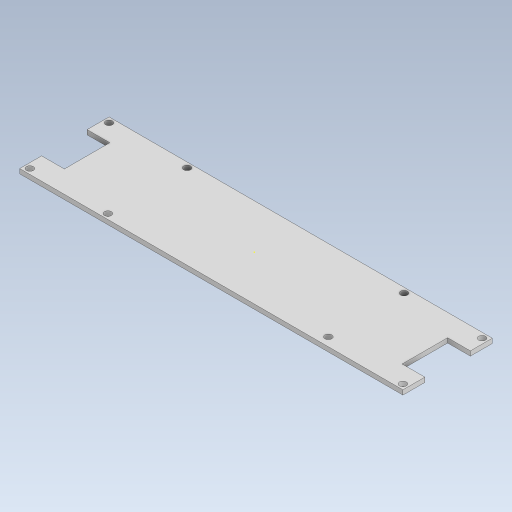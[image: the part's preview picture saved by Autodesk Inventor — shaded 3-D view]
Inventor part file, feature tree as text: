
AUTODESK INVENTOR PART (.ipt)
format: ipt  version: 2023.5 (Build 275446000, 446)  size: 306,176 bytes
history: native  units: in
note: dims shown in document units (in); Inventor stores cm internally (conversion verified against a paired STEP export)
features: extrude x4, sketch x3
ambient origin geometry x8: Origin, YZ Plane, XZ Plane, XY Plane, X Axis, Y Axis, Z Axis, Center Point
bodies: Solid1 (feature_tree)
feature tree (7):
  sketch  "Sketch1"  dims[d0=6.6339in d1=1.5472in]
  extrude  "Extrusion1"  Depth=1.5472in
  extrude  "Extrusion2"  Depth=0.0886in
  extrude  "Extrusion3"  Depth=0.0787in TaperAngle=0.0deg
  sketch  "Sketch3"  dims[d4=0.0886in d5=0.0787in d6=0.0in d7=0.0886in d8=0.0787in d9=0.0in d10=0.7874in d11=0.7874in d12=0.7874in d13=0.7874in d14=0.0787in d15=0.0in d16=0.1181in d17=1.3504in d18=0.1181in d19=0.1181in d20=1.3504in d21=0.1181in d22=0.0787in d23=0.0in]
  extrude  "Extrusion4"  Depth=0.0787in
  sketch  "Sketch2"  dims[d2=0.1181in d3=0.0886in]
